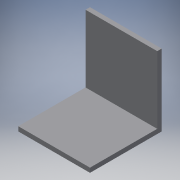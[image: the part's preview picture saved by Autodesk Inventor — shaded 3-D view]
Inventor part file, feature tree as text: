
AUTODESK INVENTOR PART (.ipt)
format: ipt  version: 2016 (Build 200138000, 138)  size: 116,736 bytes
history: native  units: in
note: dims shown in document units (in); Inventor stores cm internally (conversion verified against a paired STEP export)
features: extrude x3, sketch x3
ambient origin geometry x8: Origin, YZ Plane, XZ Plane, XY Plane, X Axis, Y Axis, Z Axis, Center Point
bodies: Solid1 (feature_tree)
feature tree (6):
  extrude  "Extrusion1"  Depth=0.125in
  extrude  "Extrusion2"  Depth=1.875in
  extrude  "Extrusion3"  Depth=0.125in
  sketch  "Sketch1"  dims[d0=1.0in d1=0.125in]
  sketch  "Sketch2"  dims[d2=0.875in d3=1.875in]
  sketch  "Sketch3"  dims[d4=2.0in d5=0.0in d6=0.25in d7=0.5in d8=0.5in d9=0.5in d10=0.5in d11=0.125in d12=0.0in d13=0.25in d14=0.25in d15=0.5in d16=0.5in d17=0.5in d18=1.5in d19=0.125in d20=0.0in]
